# Revit family: Kopfplatte I-Stiel, KI8 CPS5-2-400FT
name_source: partatom
category: Generic Models
revit_build: Autodesk Revit 2017 (Build: 20190508_0315(x64)
units: mm (PartAtom-declared; Revit-internal decimal feet)

## family parameters
Always vertical = Yes
Can host rebar = No
Cut with Voids When Loaded = No
Part Type = Normal
Room Calculation Point = No
Round Connector Dimension = Use Diameter
Shared = No
Work Plane-Based = No

## types (1)
- KI8 CPS5-2-400FT
    Article Type = KI8 CPS5-2-400FT
    GTIN = 4012195808558
    Height = 30 mm  [stored 0.0984252 ft]
    Height 1 = 150 mm
    Height 2 = 68 mm  [stored 0.223097 ft]
    Length = 397 mm  [stored 1.30249 ft]
    Length 1 = 150 mm
    Manufacturer = OBO Bettermann
    Manufacturer Art.No. = 6347032
    Material = Hot-dip galvanised
    URL = http://www.obo-bettermann.com
    Width = 100 mm  [stored 0.328084 ft]
    Width 1 = 50 mm  [stored 0.164042 ft]

note: [stored X ft] marks values corroborated as IEEE doubles in the binary element streams (Revit-internal decimal feet)

## geometry (parser evidence)
native form markers: Sweep x2
no freeform markers — native parametric forms only
